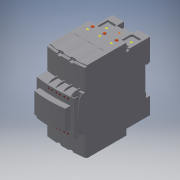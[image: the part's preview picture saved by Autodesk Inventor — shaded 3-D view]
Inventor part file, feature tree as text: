
AUTODESK INVENTOR PART (.ipt)
format: ipt  version: 2017 (Build 210142000, 142)  size: 710,656 bytes
history: native  units: in
note: dims shown in document units (in); Inventor stores cm internally (conversion verified against a paired STEP export)
features: other x5, sketch x3
ambient origin geometry x8: Origin, YZ Plane, XZ Plane, XY Plane, X Axis, Y Axis, Z Axis, Center Point
bodies: Body1 (feature_tree)
feature tree (8):
  other  "lc1d65am7_ew"
  other  "Sólido1"
  other  "cont1_1"
  other  "cont1_2"
  other  "cont1_3"
  sketch  "Boceto1"
  sketch  "Boceto2"
  sketch  "Boceto3"
